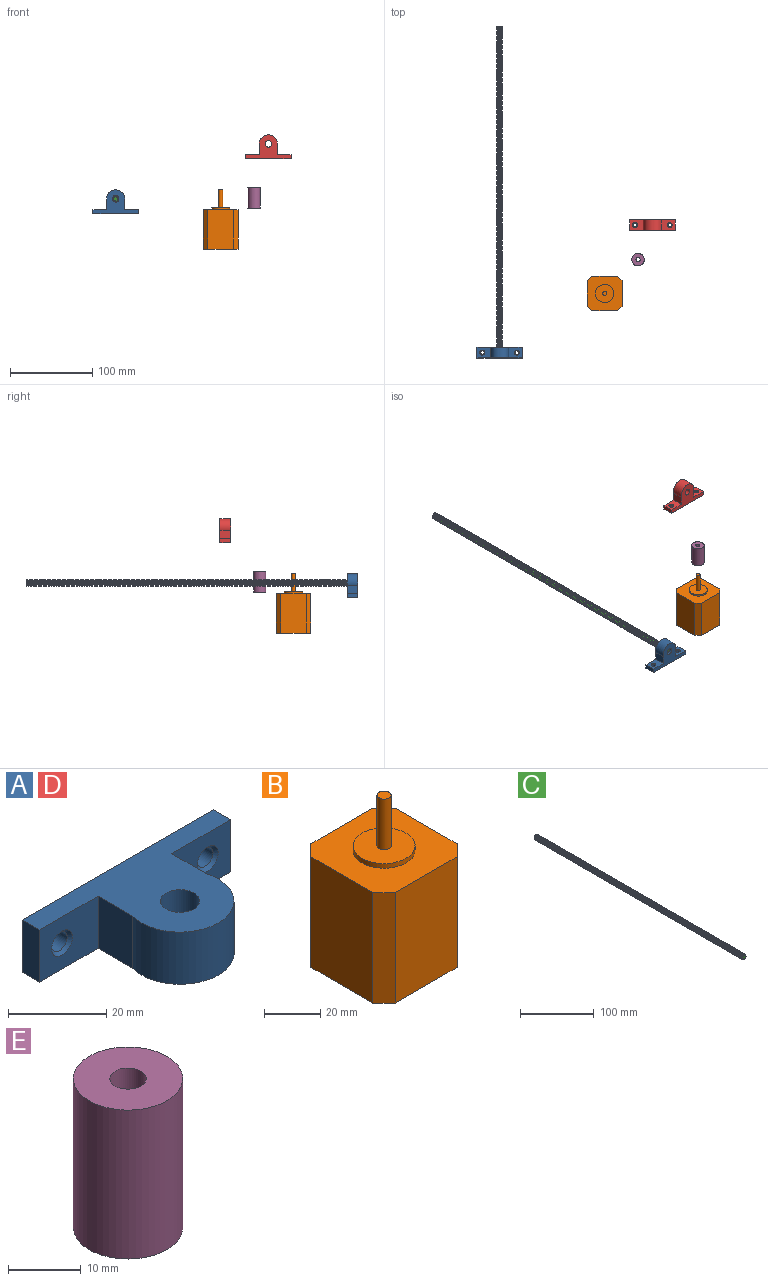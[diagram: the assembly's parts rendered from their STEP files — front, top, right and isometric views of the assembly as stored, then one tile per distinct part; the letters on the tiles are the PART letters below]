
ASSEMBLY  parts=5 mates=1
PART A: 17 faces, bbox 55x29x13 mm
  f0: plane 13x5mm, normal (-1,0,0), area 65mm2, adj f1,f10,f11,f12
  f1: plane 55x13mm, normal (0,1,0), area 683.2mm2, adj f0,f2,f11,f12,f13,f15
  f2: plane 13x5mm, normal (1,0,0), area 65mm2, adj f1,f3,f11,f12
  f3: plane 16.94x13mm, normal (0,-1,0), area 191.9mm2, adj f2,f4,f11,f12,f16
  f4: cylinder r=16.75mm len=13mm, axis (0,0,-1), area 0.4mm2, adj f3,f5,f11,f12
  f5: plane 13x9.99mm, normal (1,0,0), area 129.8mm2, adj f4,f6,f11,f12
  f6: cylinder r=11mm len=22mm, axis (0,0,-1), area 528.1mm2, adj f5,f7,f11,f12
  f7: plane 13x9.99mm, normal (-1,0,0), area 129.8mm2, adj f6,f8,f11,f12
  f8: cylinder r=16.75mm len=13mm, axis (0,0,-1), area 0.4mm2, adj f7,f10,f11,f12
  f9: cylinder r=4mm len=13mm, axis (0,0,-1), area 326.7mm2, adj f11,f12
  f10: plane 16.94x13mm, normal (0,-1,0), area 191.9mm2, adj f0,f8,f11,f12,f14
  f11: plane 55x29mm, normal (0,0,1), area 691.7mm2, adj f0,f1,f2,f3,f4,f5,f6,f7
  f12: plane 55x29mm, normal (0,0,-1), area 691.7mm2, adj f0,f1,f2,f3,f4,f5,f6,f7
  f13: cylinder r=2.25mm len=4.5mm, axis (0,-1,0), area 60.1mm2, adj f1,f14
  f14: cone r=2.25mm half-angle=45deg, axis (0,-1,0), area 17.5mm2, adj f10,f13
  f15: cylinder r=2.25mm len=4.5mm, axis (0,-1,0), area 60.1mm2, adj f1,f16
  f16: cone r=2.25mm half-angle=45deg, axis (0,-1,0), area 17.5mm2, adj f3,f15
PART B: 14 faces, bbox 42.3x42.3x72 mm
  f0: plane 48x31mm, normal (0,-1,0), area 1488mm2, adj f1,f7,f8,f9
  f1: plane 48x5.65mm, normal (-0.71,-0.71,0), area 383.5mm2, adj f0,f2,f8,f9
  f2: plane 48x31mm, normal (-1,0,0), area 1488mm2, adj f1,f3,f8,f9
  f3: plane 48x5.65mm, normal (-0.71,0.71,0), area 383.5mm2, adj f2,f4,f8,f9
  f4: plane 48x31mm, normal (0,1,0), area 1488mm2, adj f3,f5,f8,f9
  f5: plane 48x5.65mm, normal (0.71,0.71,0), area 383.5mm2, adj f4,f6,f8,f9
  f6: plane 48x31mm, normal (1,0,0), area 1488mm2, adj f5,f7,f8,f9
  f7: plane 48x5.65mm, normal (0.71,-0.71,0), area 383.5mm2, adj f0,f6,f8,f9
  f8: plane 42.3x42.3mm, normal (0,0,-1), area 1725.4mm2, adj f0,f1,f2,f3,f4,f5,f6,f7
  f9: plane 42.3x42.3mm, normal (0,0,1), area 1345.3mm2, adj f0,f1,f2,f3,f4,f5,f6,f7
  f10: cylinder r=11mm len=22mm, axis (0,0,-1), area 138.2mm2, adj f9,f11
  f11: plane 22x22mm, normal (0,0,1), area 360.5mm2, adj f10,f12
  f12: cylinder r=2.5mm len=22mm, axis (0,0,-1), area 345.6mm2, adj f11,f13
  f13: plane 5x5mm, normal (0,0,1), area 19.6mm2, adj f12
PART C: 8 faces, bbox 10.5x403.1x9.2 mm
  f0: cylinder r=4mm len=399.2mm, axis (0,-1,0), area 23189.4mm2, adj f1,f3,f4,f5,f6,f7
  f1: plane 9.24x8.52mm, normal (0,1,0), area 41.8mm2, adj f0,f3,f4
  f2: plane 6.7x6.7mm, normal (0,-1,0), area 30.3mm2, adj f5,f6,f7
  f3: plane 1.65x0.95mm, normal (1,0,0), area 0.8mm2, adj f0,f1,f6
  f4: bspline ~400.95x9.24mm, area 7580.4mm2, adj f0,f1,f5,f6
  f5: plane 1.65x0.95mm, normal (-1,0,0), area 0.5mm2, adj f0,f2,f4,f7
  f6: bspline ~400.95x9.24mm, area 7584.3mm2, adj f0,f2,f3,f4,f7
  f7: cone r=3.2mm half-angle=45deg, axis (0,1,0), area 11mm2, adj f0,f2,f5,f6
PART D: same geometry as A
PART E: 6 faces, bbox 15x15x25 mm
  f0: cylinder r=7.5mm len=25mm, axis (0,0,-1), area 1178.1mm2, adj f1,f2
  f1: plane 15x15mm, normal (0,0,1), area 157.1mm2, adj f0,f3
  f2: plane 15x15mm, normal (0,0,-1), area 126.4mm2, adj f0,f5
  f3: cylinder r=2.5mm len=12.5mm, axis (0,0,-1), area 196.3mm2, adj f1,f4
  f4: plane 8x8mm, normal (0,0,-1), area 30.6mm2, adj f3,f5
  f5: cylinder r=4mm len=12.5mm, axis (0,0,-1), area 314.2mm2, adj f2,f4
PLACE A rot(axis=(-1,0,0),90deg) t=(-161.33,-123.44,-28.02)mm
PLACE B t=(-22.38,-19.63,3.45)mm
PLACE C t=(-195.8,-120.39,-29.3)mm
PLACE D rot(axis=(-1,0,0),90deg) t=(24.18,31.28,38.62)mm
PLACE E t=(14.02,37,5.37)mm
MATE cylindrical C.f0 <-> A.f4  axis (0,-1,0) through (-195.8,-120.39,16.58)mm
